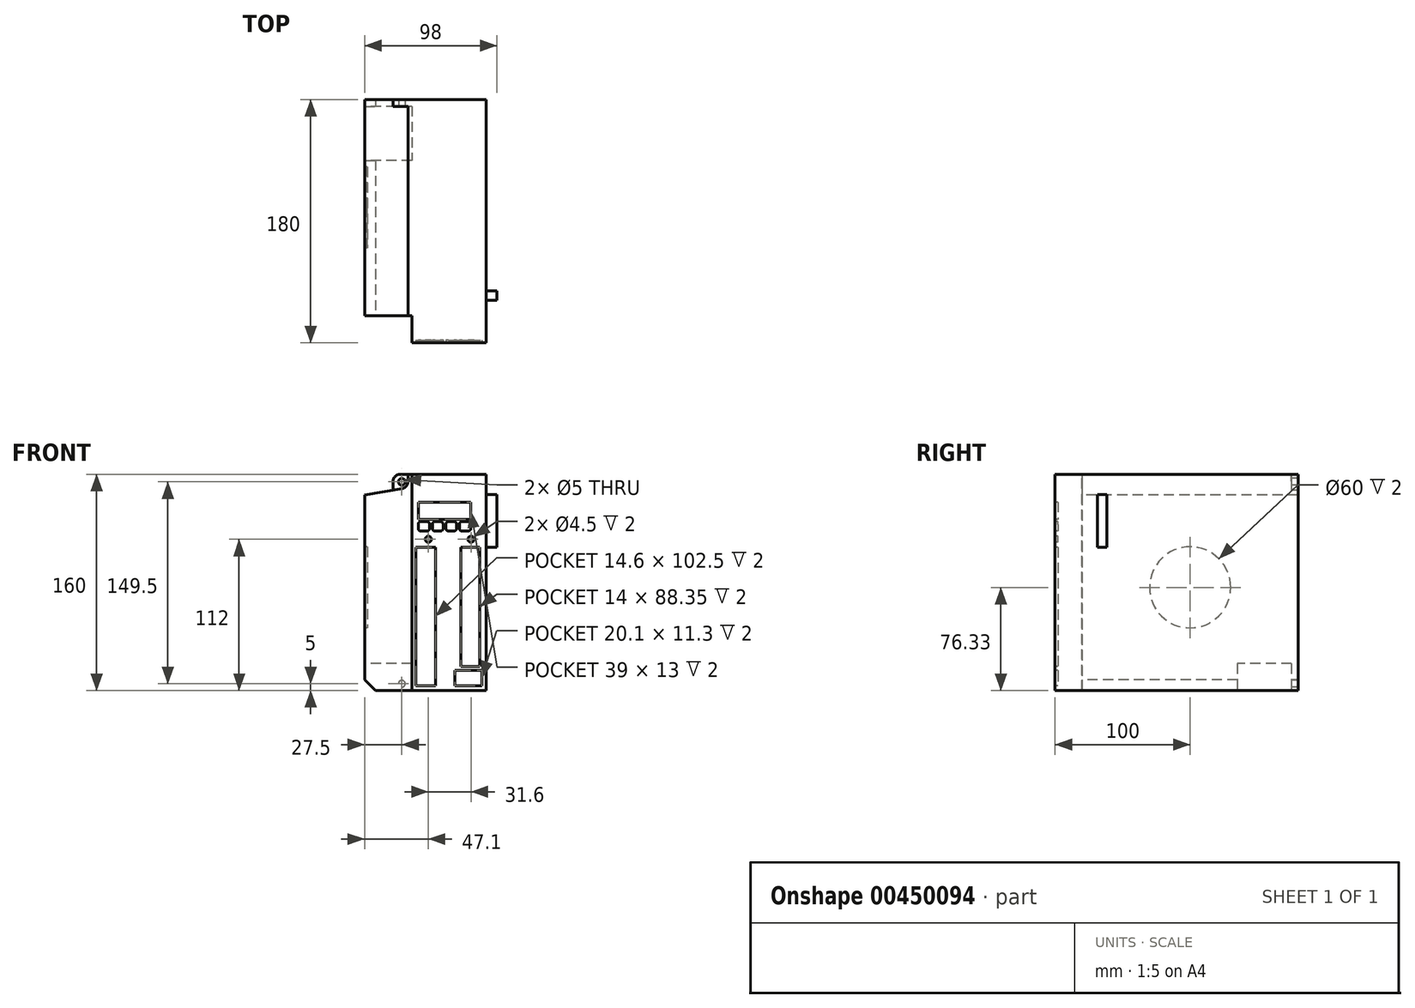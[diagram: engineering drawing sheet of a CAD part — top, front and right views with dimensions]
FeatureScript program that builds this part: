
annotation { "Feature Type Name" : "Feature", "Feature Type Description" : "" }
export const myFeature = defineFeature(function(context is Context, id is Id, definition is map)
    precondition{}
    {
        {
            var Q0;
            Q0=qCreatedBy(makeId("Front.planeOp"),FACE);
            var sketch = newSketch(context, id + "F0", { "sketchPlane" : qUnion([Q0])});
            skLineSegment(sketch, "E0.bottom", {"start": v(0, 0) * mm, "end": v(55, 0) * mm});
            skLineSegment(sketch, "E0.top", {"start": v(0, 160) * mm, "end": v(55, 160) * mm});
            skLineSegment(sketch, "E0.left", {"start": v(0, 0) * mm, "end": v(0, 160) * mm});
            skLineSegment(sketch, "E0.right", {"start": v(55, 0) * mm, "end": v(55, 160) * mm});
            skSolve(sketch);
        }
        {
            var Q0;
            Q0=makeQuery(id+"F0.imprint","IMPRINT",FACE,{"disambiguationData":[TD([[makeQuery(id+"F0.imprint","IMPRINT",EDGE,{"derivedFrom":sQuery(id+"F0.wireOp",EDGE,"E0.bottom")}),1.0]])]});
            extrude(context, id + "F1", {"entities" : qUnion([Q0]), "oppositeDirection" : true, "depth" : 20 * mm});
        }
        {
            var Q0;
            Q0=makeQuery(id+"F1.opExtrude","CAP_FACE",FACE,{"disambiguationData":[OSD([sQuery(id+"F0.wireOp",EDGE,"E0.bottom"),sQuery(id+"F0.wireOp",EDGE,"E0.top"),sQuery(id+"F0.wireOp",EDGE,"E0.left"),sQuery(id+"F0.wireOp",EDGE,"E0.right")])],"isStart":false});
            var sketch = newSketch(context, id + "F2", { "sketchPlane" : qUnion([Q0])});
            skLineSegment(sketch, "E1", {"start": v(-55, 160) * mm, "end": v(3, 160) * mm});
            skLineSegment(sketch, "E2", {"start": v(3, 160) * mm, "end": v(3, 154.5) * mm});
            skLineSegment(sketch, "E3", {"start": v(7.13, 149.57) * mm, "end": v(35, 144.66) * mm});
            skLineSegment(sketch, "E4", {"start": v(35, 144.66) * mm, "end": v(35, 8) * mm});
            skLineSegment(sketch, "E5", {"start": v(35, 8) * mm, "end": v(27, 0) * mm});
            skLineSegment(sketch, "E6", {"start": v(27, 0) * mm, "end": v(-55, 0) * mm});
            skLineSegment(sketch, "E7", {"start": v(-55, 0) * mm, "end": v(-55, 160) * mm});
            skPoint(sketch, "E8.visualSharp", {"position": v(3, 150.3) * mm});
            skArc(sketch, "E8.filletArc", {"start": v(3, 154.5) * mm, "mid": v(4.17, 151.28) * mm, "end": v(7.13, 149.57) * mm});
            skSolve(sketch);
        }
        {
            var Q0;
            {var subQ0=sQuery(id+"F2.wireOp",EDGE,"E2");Q0=makeQuery(id+"F2.imprint","IMPRINT",FACE,{"disambiguationData":[TD([[makeQuery(id+"F2.imprint","IMPRINT",EDGE,{"derivedFrom":subQ0}),-1.0]])]});}
            var Q1;
            {var subQ2=sQuery(id+"F2.wireOp",EDGE,"E7");Q1=makeQuery(id+"F2.imprint","IMPRINT",FACE,{"disambiguationData":[TD([[makeQuery(id+"F2.imprint","IMPRINT",EDGE,{"derivedFrom":subQ2}),-1.0]])]});}
            extrude(context, id + "F3", {"entities" : qUnion([Q0, Q1]), "operationType" : NewBodyOperationType.ADD, "depth" : 155 * mm});
        }
        {
            var Q0;
            Q0=makeQuery(id+"F3.opExtrude","CAP_FACE",FACE,{"disambiguationData":[OSD([sQuery(id+"F2.wireOp",EDGE,"E1"),sQuery(id+"F2.wireOp",EDGE,"E2"),sQuery(id+"F2.wireOp",EDGE,"E3"),sQuery(id+"F2.wireOp",EDGE,"E4"),sQuery(id+"F2.wireOp",EDGE,"E5"),sQuery(id+"F2.wireOp",EDGE,"E6"),sQuery(id+"F2.wireOp",EDGE,"E7")])],"isStart":false});
            var sketch = newSketch(context, id + "F4", { "sketchPlane" : qUnion([Q0])});
            skLineSegment(sketch, "E9", {"start": v(-55, 160) * mm, "end": v(9, 160) * mm});
            skLineSegment(sketch, "E10", {"start": v(14, 155) * mm, "end": v(14, 148.36) * mm});
            skLineSegment(sketch, "E11", {"start": v(14, 148.36) * mm, "end": v(35, 144.66) * mm});
            skLineSegment(sketch, "E12", {"start": v(35, 144.66) * mm, "end": v(35, 8) * mm});
            skLineSegment(sketch, "E13", {"start": v(35, 8) * mm, "end": v(27, 0) * mm});
            skLineSegment(sketch, "E14", {"start": v(27, 0) * mm, "end": v(-55, 0) * mm});
            skLineSegment(sketch, "E15", {"start": v(-55, 0) * mm, "end": v(-55, 160) * mm});
            skCircle(sketch, "E16", {"center": v(7.5, 154.5) * mm, "radius": 2.5 * mm});
            skPoint(sketch, "E16.centerSnap0", {"position": v(3, 157.25) * mm});
            skCircle(sketch, "E17", {"center": v(7.5, 5) * mm, "radius": 2.5 * mm});
            skPoint(sketch, "E18.visualSharp", {"position": v(14, 160) * mm});
            skArc(sketch, "E18.filletArc", {"start": v(14, 155) * mm, "mid": v(12.54, 158.54) * mm, "end": v(9, 160) * mm});
            skSolve(sketch);
        }
        {
            var Q0;
            {var subQ4=sQuery(id+"F4.wireOp",EDGE,"E18.filletArc");Q0=makeQuery(id+"F4.imprint","IMPRINT",FACE,{"disambiguationData":[TD([[makeQuery(id+"F4.imprint","IMPRINT",EDGE,{"derivedFrom":subQ4}),1.0]])]});}
            var Q1;
            {var subQ7=sQuery(id+"F4.wireOp",EDGE,"E11");Q1=makeQuery(id+"F4.imprint","IMPRINT",FACE,{"disambiguationData":[TD([[makeQuery(id+"F4.imprint","IMPRINT",EDGE,{"derivedFrom":subQ7}),-1.0]])]});}
            extrude(context, id + "F5", {"entities" : qUnion([Q0, Q1]), "operationType" : NewBodyOperationType.ADD, "depth" : 5 * mm});
        }
        {
            var Q0;
            Q0=makeQuery(id+"F5.boolean.opBoolean","MERGE",FACE,{"derivedFrom":[makeQuery(id+"F3.boolean.opBoolean","MERGE",FACE,{"derivedFrom":[makeQuery(id+"F1.opExtrude","SWEPT_FACE",FACE,{"disambiguationData":[OSD([sQuery(id+"F0.wireOp",EDGE,"E0.right")])]}),makeQuery(id+"F3.opExtrude","SWEPT_FACE",FACE,{"disambiguationData":[OSD([sQuery(id+"F2.wireOp",EDGE,"E7")])]})]}),makeQuery(id+"F5.opExtrude","SWEPT_FACE",FACE,{"disambiguationData":[OSD([sQuery(id+"F4.wireOp",EDGE,"E15")])]})]});
            var sketch = newSketch(context, id + "F6", { "sketchPlane" : qUnion([Q0])});
            skLineSegment(sketch, "E19.bottom", {"start": v(31.5, 106) * mm, "end": v(38.5, 106) * mm});
            skLineSegment(sketch, "E19.top", {"start": v(31.5, 145) * mm, "end": v(38.5, 145) * mm});
            skLineSegment(sketch, "E19.left", {"start": v(31.5, 106) * mm, "end": v(31.5, 145) * mm});
            skLineSegment(sketch, "E19.right", {"start": v(38.5, 106) * mm, "end": v(38.5, 145) * mm});
            skSolve(sketch);
        }
        {
            var Q0;
            Q0=makeQuery(id+"F6.imprint","IMPRINT",FACE,{"disambiguationData":[TD([[makeQuery(id+"F6.imprint","IMPRINT",EDGE,{"derivedFrom":sQuery(id+"F6.wireOp",EDGE,"E19.bottom")}),1.0]])]});
            extrude(context, id + "F7", {"entities" : qUnion([Q0]), "operationType" : NewBodyOperationType.ADD, "depth" : 8 * mm});
        }
        {
            var Q0;
            Q0=makeQuery(id+"F1.opExtrude","CAP_FACE",FACE,{"disambiguationData":[OSD([sQuery(id+"F0.wireOp",EDGE,"E0.bottom"),sQuery(id+"F0.wireOp",EDGE,"E0.top"),sQuery(id+"F0.wireOp",EDGE,"E0.left"),sQuery(id+"F0.wireOp",EDGE,"E0.right")])],"isStart":true});
            var sketch = newSketch(context, id + "F8", { "sketchPlane" : qUnion([Q0])});
            skLineSegment(sketch, "E20.bottom", {"start": v(4.6, 139.5) * mm, "end": v(43.6, 139.5) * mm});
            skLineSegment(sketch, "E20.top", {"start": v(4.6, 126.5) * mm, "end": v(43.6, 126.5) * mm});
            skLineSegment(sketch, "E20.left", {"start": v(4.6, 139.5) * mm, "end": v(4.6, 126.5) * mm});
            skLineSegment(sketch, "E20.right", {"start": v(43.6, 139.5) * mm, "end": v(43.6, 126.5) * mm});
            skLineSegment(sketch, "E21.bottom", {"start": v(6.6, 125) * mm, "end": v(11.1, 125) * mm});
            skLineSegment(sketch, "E21.top", {"start": v(6.6, 118) * mm, "end": v(11.1, 118) * mm});
            skLineSegment(sketch, "E21.left", {"start": v(4.6, 123) * mm, "end": v(4.6, 120) * mm});
            skLineSegment(sketch, "E21.right", {"start": v(13.1, 123) * mm, "end": v(13.1, 120) * mm});
            skLineSegment(sketch, "E22.bottom", {"start": v(17.1, 118) * mm, "end": v(21.1, 118) * mm});
            skLineSegment(sketch, "E22.top", {"start": v(17.1, 125) * mm, "end": v(21.1, 125) * mm});
            skLineSegment(sketch, "E22.left", {"start": v(15.1, 120) * mm, "end": v(15.1, 123) * mm});
            skLineSegment(sketch, "E22.right", {"start": v(23.1, 120) * mm, "end": v(23.1, 123) * mm});
            skLineSegment(sketch, "E23.bottom", {"start": v(27.1, 118) * mm, "end": v(31.1, 118) * mm});
            skLineSegment(sketch, "E23.top", {"start": v(27.1, 125) * mm, "end": v(31.1, 125) * mm});
            skLineSegment(sketch, "E23.left", {"start": v(25.1, 120) * mm, "end": v(25.1, 123) * mm});
            skLineSegment(sketch, "E23.right", {"start": v(33.1, 120) * mm, "end": v(33.1, 123) * mm});
            skLineSegment(sketch, "E24.bottom", {"start": v(37.1, 118) * mm, "end": v(41.6, 118) * mm});
            skLineSegment(sketch, "E24.top", {"start": v(37.1, 125) * mm, "end": v(41.6, 125) * mm});
            skLineSegment(sketch, "E24.left", {"start": v(35.1, 120) * mm, "end": v(35.1, 123) * mm});
            skLineSegment(sketch, "E24.right", {"start": v(43.6, 120) * mm, "end": v(43.6, 123) * mm});
            skPoint(sketch, "E25.visualSharp", {"position": v(15.1, 125) * mm});
            skArc(sketch, "E25.filletArc", {"start": v(17.1, 125) * mm, "mid": v(15.69, 124.41) * mm, "end": v(15.1, 123) * mm});
            skPoint(sketch, "E26.visualSharp", {"position": v(23.1, 125) * mm});
            skArc(sketch, "E26.filletArc", {"start": v(23.1, 123) * mm, "mid": v(22.51, 124.41) * mm, "end": v(21.1, 125) * mm});
            skPoint(sketch, "E27.visualSharp", {"position": v(23.1, 118) * mm});
            skArc(sketch, "E27.filletArc", {"start": v(21.1, 118) * mm, "mid": v(22.51, 118.59) * mm, "end": v(23.1, 120) * mm});
            skPoint(sketch, "E28.visualSharp", {"position": v(15.1, 118) * mm});
            skArc(sketch, "E28.filletArc", {"start": v(15.1, 120) * mm, "mid": v(15.69, 118.59) * mm, "end": v(17.1, 118) * mm});
            skPoint(sketch, "E29.visualSharp", {"position": v(25.1, 125) * mm});
            skArc(sketch, "E29.filletArc", {"start": v(27.1, 125) * mm, "mid": v(25.69, 124.41) * mm, "end": v(25.1, 123) * mm});
            skPoint(sketch, "E30.visualSharp", {"position": v(33.1, 125) * mm});
            skArc(sketch, "E30.filletArc", {"start": v(33.1, 123) * mm, "mid": v(32.51, 124.41) * mm, "end": v(31.1, 125) * mm});
            skPoint(sketch, "E31.visualSharp", {"position": v(33.1, 118) * mm});
            skArc(sketch, "E31.filletArc", {"start": v(31.1, 118) * mm, "mid": v(32.51, 118.59) * mm, "end": v(33.1, 120) * mm});
            skPoint(sketch, "E32.visualSharp", {"position": v(25.1, 118) * mm});
            skArc(sketch, "E32.filletArc", {"start": v(25.1, 120) * mm, "mid": v(25.69, 118.59) * mm, "end": v(27.1, 118) * mm});
            skPoint(sketch, "E33.visualSharp", {"position": v(35.1, 125) * mm});
            skArc(sketch, "E33.filletArc", {"start": v(37.1, 125) * mm, "mid": v(35.69, 124.41) * mm, "end": v(35.1, 123) * mm});
            skPoint(sketch, "E34.visualSharp", {"position": v(35.1, 118) * mm});
            skArc(sketch, "E34.filletArc", {"start": v(35.1, 120) * mm, "mid": v(35.69, 118.59) * mm, "end": v(37.1, 118) * mm});
            skPoint(sketch, "E35.visualSharp", {"position": v(13.1, 125) * mm});
            skArc(sketch, "E35.filletArc", {"start": v(13.1, 123) * mm, "mid": v(12.51, 124.41) * mm, "end": v(11.1, 125) * mm});
            skPoint(sketch, "E36.visualSharp", {"position": v(13.1, 118) * mm});
            skArc(sketch, "E36.filletArc", {"start": v(11.1, 118) * mm, "mid": v(12.51, 118.59) * mm, "end": v(13.1, 120) * mm});
            skPoint(sketch, "E37.visualSharp", {"position": v(43.6, 125) * mm});
            skArc(sketch, "E37.filletArc", {"start": v(43.6, 123) * mm, "mid": v(43.01, 124.41) * mm, "end": v(41.6, 125) * mm});
            skPoint(sketch, "E38.visualSharp", {"position": v(43.6, 118) * mm});
            skArc(sketch, "E38.filletArc", {"start": v(41.6, 118) * mm, "mid": v(43.01, 118.59) * mm, "end": v(43.6, 120) * mm});
            skPoint(sketch, "E39.visualSharp", {"position": v(4.6, 125) * mm});
            skArc(sketch, "E39.filletArc", {"start": v(6.6, 125) * mm, "mid": v(5.19, 124.41) * mm, "end": v(4.6, 123) * mm});
            skPoint(sketch, "E40.visualSharp", {"position": v(4.6, 118) * mm});
            skArc(sketch, "E40.filletArc", {"start": v(4.6, 120) * mm, "mid": v(5.19, 118.59) * mm, "end": v(6.6, 118) * mm});
            skCircle(sketch, "E41", {"center": v(12.1, 112) * mm, "radius": 2.25 * mm});
            skCircle(sketch, "E42", {"center": v(43.7, 112) * mm, "radius": 2.25 * mm});
            skLineSegment(sketch, "E43.bottom", {"start": v(36.3, 106) * mm, "end": v(50.3, 106) * mm});
            skLineSegment(sketch, "E43.top", {"start": v(36.3, 17.65) * mm, "end": v(50.3, 17.65) * mm});
            skLineSegment(sketch, "E43.left", {"start": v(36.3, 106) * mm, "end": v(36.3, 17.65) * mm});
            skLineSegment(sketch, "E43.right", {"start": v(50.3, 106) * mm, "end": v(50.3, 17.65) * mm});
            skLineSegment(sketch, "E44.bottom", {"start": v(31.8, 14.85) * mm, "end": v(51.9, 14.85) * mm});
            skLineSegment(sketch, "E44.top", {"start": v(31.8, 3.55) * mm, "end": v(51.9, 3.55) * mm});
            skLineSegment(sketch, "E44.left", {"start": v(31.8, 14.85) * mm, "end": v(31.8, 3.55) * mm});
            skLineSegment(sketch, "E44.right", {"start": v(51.9, 14.85) * mm, "end": v(51.9, 3.55) * mm});
            skLineSegment(sketch, "E45.bottom", {"start": v(2.9, 106.05) * mm, "end": v(17.5, 106.05) * mm});
            skLineSegment(sketch, "E45.top", {"start": v(2.9, 3.55) * mm, "end": v(17.5, 3.55) * mm});
            skLineSegment(sketch, "E45.left", {"start": v(2.9, 106.05) * mm, "end": v(2.9, 3.55) * mm});
            skLineSegment(sketch, "E45.right", {"start": v(17.5, 106.05) * mm, "end": v(17.5, 3.55) * mm});
            skSolve(sketch);
        }
        {
            var Q0;
            Q0=makeQuery(id+"F8.imprint","IMPRINT",FACE,{"disambiguationData":[TD([[makeQuery(id+"F8.imprint","IMPRINT",EDGE,{"derivedFrom":sQuery(id+"F8.wireOp",EDGE,"E45.bottom")}),-1.0]])]});
            var Q1;
            Q1=makeQuery(id+"F8.imprint","IMPRINT",FACE,{"disambiguationData":[TD([[makeQuery(id+"F8.imprint","IMPRINT",EDGE,{"derivedFrom":sQuery(id+"F8.wireOp",EDGE,"E43.bottom")}),-1.0]])]});
            var Q2;
            Q2=makeQuery(id+"F8.imprint","IMPRINT",FACE,{"disambiguationData":[TD([[makeQuery(id+"F8.imprint","IMPRINT",EDGE,{"derivedFrom":sQuery(id+"F8.wireOp",EDGE,"E44.bottom")}),-1.0]])]});
            var Q3;
            Q3=makeQuery(id+"F8.imprint","IMPRINT",FACE,{"disambiguationData":[TD([[makeQuery(id+"F8.imprint","IMPRINT",EDGE,{"derivedFrom":sQuery(id+"F8.wireOp",EDGE,"E20.bottom")}),-1.0]])]});
            var Q4;
            Q4=makeQuery(id+"F8.imprint","IMPRINT",FACE,{"disambiguationData":[TD([[makeQuery(id+"F8.imprint","IMPRINT",EDGE,{"derivedFrom":sQuery(id+"F8.wireOp",EDGE,"E21.bottom")}),-1.0]])]});
            var Q5;
            Q5=makeQuery(id+"F8.imprint","IMPRINT",FACE,{"disambiguationData":[TD([[makeQuery(id+"F8.imprint","IMPRINT",EDGE,{"derivedFrom":sQuery(id+"F8.wireOp",EDGE,"E22.bottom")}),1.0]])]});
            var Q6;
            Q6=makeQuery(id+"F8.imprint","IMPRINT",FACE,{"disambiguationData":[TD([[makeQuery(id+"F8.imprint","IMPRINT",EDGE,{"derivedFrom":sQuery(id+"F8.wireOp",EDGE,"E23.bottom")}),1.0]])]});
            var Q7;
            Q7=makeQuery(id+"F8.imprint","IMPRINT",FACE,{"disambiguationData":[TD([[makeQuery(id+"F8.imprint","IMPRINT",EDGE,{"derivedFrom":sQuery(id+"F8.wireOp",EDGE,"E24.bottom")}),1.0]])]});
            var Q8;
            Q8=makeQuery(id+"F8.imprint","IMPRINT",FACE,{"disambiguationData":[TD([[makeQuery(id+"F8.imprint","IMPRINT",EDGE,{"derivedFrom":sQuery(id+"F8.wireOp",EDGE,"E42")}),1.0]])]});
            var Q9;
            Q9=makeQuery(id+"F8.imprint","IMPRINT",FACE,{"disambiguationData":[TD([[makeQuery(id+"F8.imprint","IMPRINT",EDGE,{"derivedFrom":sQuery(id+"F8.wireOp",EDGE,"E41")}),1.0]])]});
            extrude(context, id + "F9", {"entities" : qUnion([Q0, Q1, Q2, Q3, Q4, Q5, Q6, Q7, Q8, Q9]), "operationType" : NewBodyOperationType.REMOVE, "oppositeDirection" : true, "depth" : 2 * mm});
        }
        {
            var Q0;
            Q0=makeQuery(id+"F5.boolean.opBoolean","MERGE",FACE,{"derivedFrom":[makeQuery(id+"F3.opExtrude","SWEPT_FACE",FACE,{"disambiguationData":[OSD([sQuery(id+"F2.wireOp",EDGE,"E4")])]}),makeQuery(id+"F5.opExtrude","SWEPT_FACE",FACE,{"disambiguationData":[OSD([sQuery(id+"F4.wireOp",EDGE,"E12")])]})]});
            var sketch = newSketch(context, id + "F10", { "sketchPlane" : qUnion([Q0])});
            skLineSegment(sketch, "E46.bottom", {"start": v(-175, 20) * mm, "end": v(-135, 20) * mm});
            skLineSegment(sketch, "E46.top", {"start": v(-175, 0) * mm, "end": v(-135, 0) * mm});
            skLineSegment(sketch, "E46.left", {"start": v(-175, 20) * mm, "end": v(-175, 0) * mm});
            skLineSegment(sketch, "E46.right", {"start": v(-135, 20) * mm, "end": v(-135, 0) * mm});
            skSolve(sketch);
        }
        {
            var Q0;
            {var subQ0=sQuery(id+"F10.wireOp",EDGE,"E46.bottom");Q0=makeQuery(id+"F10.imprint","IMPRINT",FACE,{"disambiguationData":[TD([[makeQuery(id+"F10.imprint","IMPRINT",EDGE,{"derivedFrom":subQ0}),-1.0]])]});}
            var Q1;
            {var subQ0=sQuery(id+"F10.wireOp",EDGE,"E46.top");Q1=makeQuery(id+"F10.imprint","IMPRINT",FACE,{"disambiguationData":[TD([[makeQuery(id+"F10.imprint","IMPRINT",EDGE,{"derivedFrom":subQ0}),1.0]])]});}
            extrude(context, id + "F11", {"entities" : qUnion([Q0, Q1]), "operationType" : NewBodyOperationType.REMOVE, "oppositeDirection" : true, "depth" : 35 * mm});
        }
        {
            var Q0;
            Q0=makeQuery(id+"F5.boolean.opBoolean","MERGE",FACE,{"derivedFrom":[makeQuery(id+"F3.opExtrude","SWEPT_FACE",FACE,{"disambiguationData":[OSD([sQuery(id+"F2.wireOp",EDGE,"E4")])]}),makeQuery(id+"F5.opExtrude","SWEPT_FACE",FACE,{"disambiguationData":[OSD([sQuery(id+"F4.wireOp",EDGE,"E12")])]})]});
            var sketch = newSketch(context, id + "F12", { "sketchPlane" : qUnion([Q0])});
            skCircle(sketch, "E47", {"center": v(-100, 76.33) * mm, "radius": 30 * mm});
            skPoint(sketch, "E47.centerSnap0", {"position": v(-100, 144.66) * mm});
            skPoint(sketch, "E47.centerSnap1", {"position": v(-180, 76.33) * mm});
            skSolve(sketch);
        }
        {
            var Q0;
            Q0=makeQuery(id+"F12.imprint","IMPRINT",FACE,{"disambiguationData":[TD([[makeQuery(id+"F12.imprint","IMPRINT",EDGE,{"derivedFrom":sQuery(id+"F12.wireOp",EDGE,"E47")}),1.0]])]});
            extrude(context, id + "F13", {"entities" : qUnion([Q0]), "operationType" : NewBodyOperationType.REMOVE, "oppositeDirection" : true, "depth" : 2 * mm});
        }
    });
